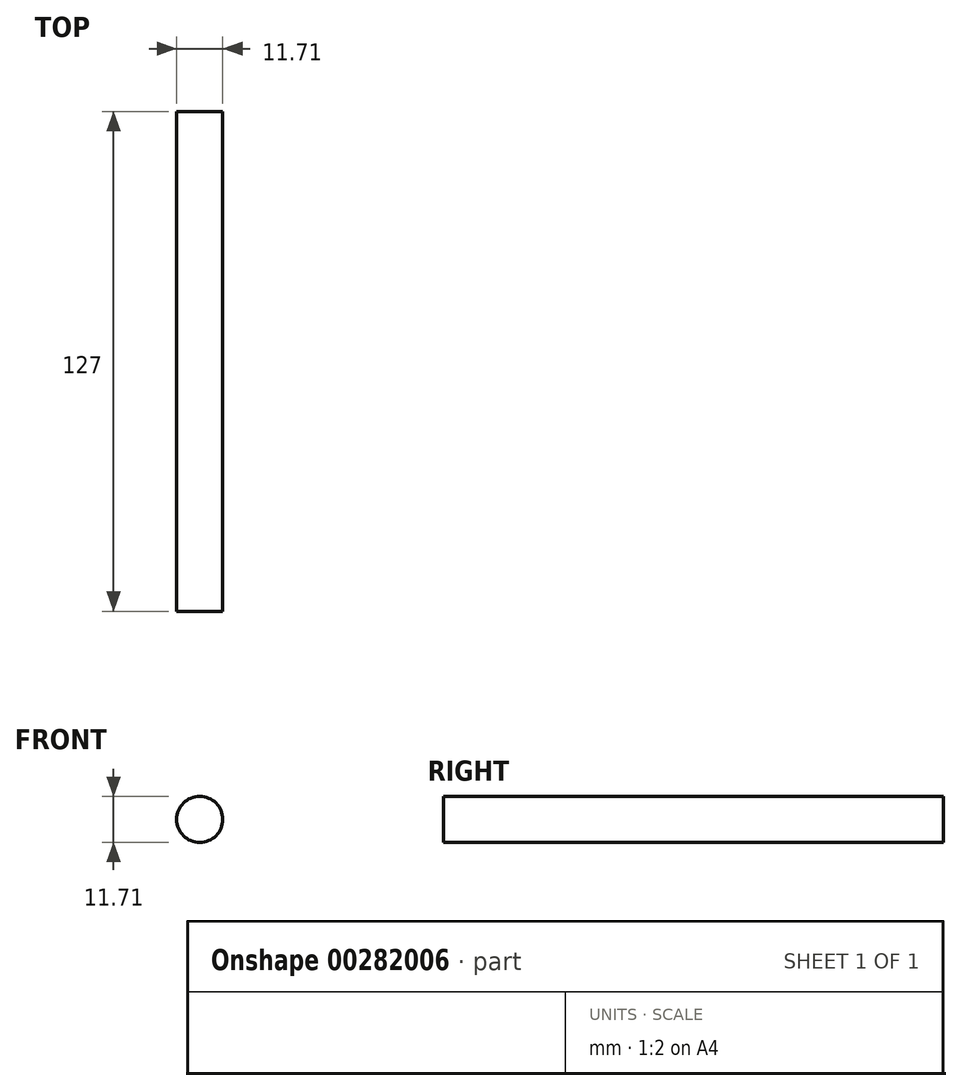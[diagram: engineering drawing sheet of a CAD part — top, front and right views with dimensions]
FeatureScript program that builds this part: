
annotation { "Feature Type Name" : "Feature", "Feature Type Description" : "" }
export const myFeature = defineFeature(function(context is Context, id is Id, definition is map)
    precondition{}
    {
        {
            var Q0;
            Q0=qCreatedBy(makeId("Front.planeOp"),FACE);
            var sketch = newSketch(context, id + "F0", { "sketchPlane" : qUnion([Q0])});
            skCircle(sketch, "E0", {"center": v(-40, 27.67) * mm, "radius": 5.85 * mm});
            skSolve(sketch);
        }
        {
            var Q0;
            Q0 = qSketchRegion(id + "F0", true);
            extrude(context, id + "F1", {"entities" : qUnion([Q0]), "depth" : 127 * mm});
        }
    });
